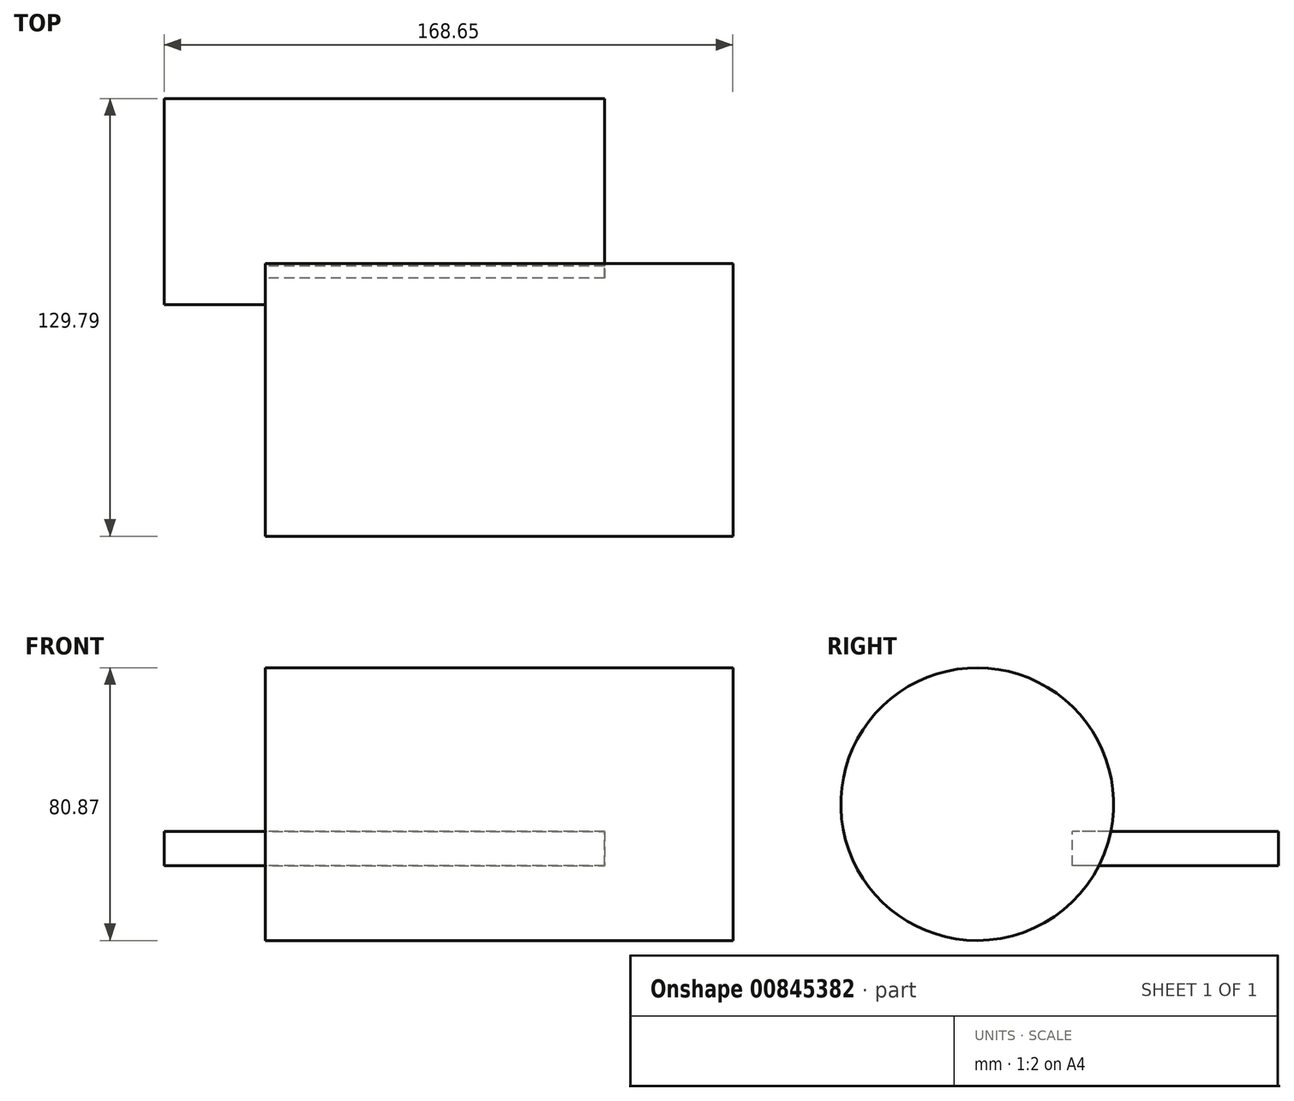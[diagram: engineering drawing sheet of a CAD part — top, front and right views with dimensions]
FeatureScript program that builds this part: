
annotation { "Feature Type Name" : "Feature", "Feature Type Description" : "" }
export const myFeature = defineFeature(function(context is Context, id is Id, definition is map)
    precondition{}
    {
        {
            var Q0;
            Q0=qCreatedBy(makeId("Right.planeOp"),FACE);
            var sketch = newSketch(context, id + "F0", { "sketchPlane" : qUnion([Q0])});
            skCircle(sketch, "E0", {"center": v(56.26, 18.2) * mm, "radius": 40.44 * mm});
            skSolve(sketch);
        }
        {
            var Q0;
            Q0 = qSketchRegion(id + "F0", true);
            extrude(context, id + "F1", {"entities" : qUnion([Q0]), "depth" : 138.68 * mm, "offsetDistance" : 25.4 * mm});
        }
        {
            var Q0;
            Q0=qCreatedBy(makeId("Top.planeOp"),FACE);
            var sketch = newSketch(context, id + "F2", { "sketchPlane" : qUnion([Q0])});
            skLineSegment(sketch, "E1.bottom", {"start": v(-29.97, 145.61) * mm, "end": v(100.64, 145.61) * mm});
            skLineSegment(sketch, "E1.top", {"start": v(-29.97, 84.5) * mm, "end": v(100.64, 84.5) * mm});
            skLineSegment(sketch, "E1.left", {"start": v(-29.97, 145.61) * mm, "end": v(-29.97, 84.5) * mm});
            skLineSegment(sketch, "E1.right", {"start": v(100.64, 145.61) * mm, "end": v(100.64, 84.5) * mm});
            skSolve(sketch);
        }
        {
            var Q0;
            Q0 = qSketchRegion(id + "F2", true);
            extrude(context, id + "F3", {"entities" : qUnion([Q0]), "operationType" : NewBodyOperationType.ADD, "depth" : 10.16 * mm, "offsetDistance" : 25.4 * mm});
        }
    });
